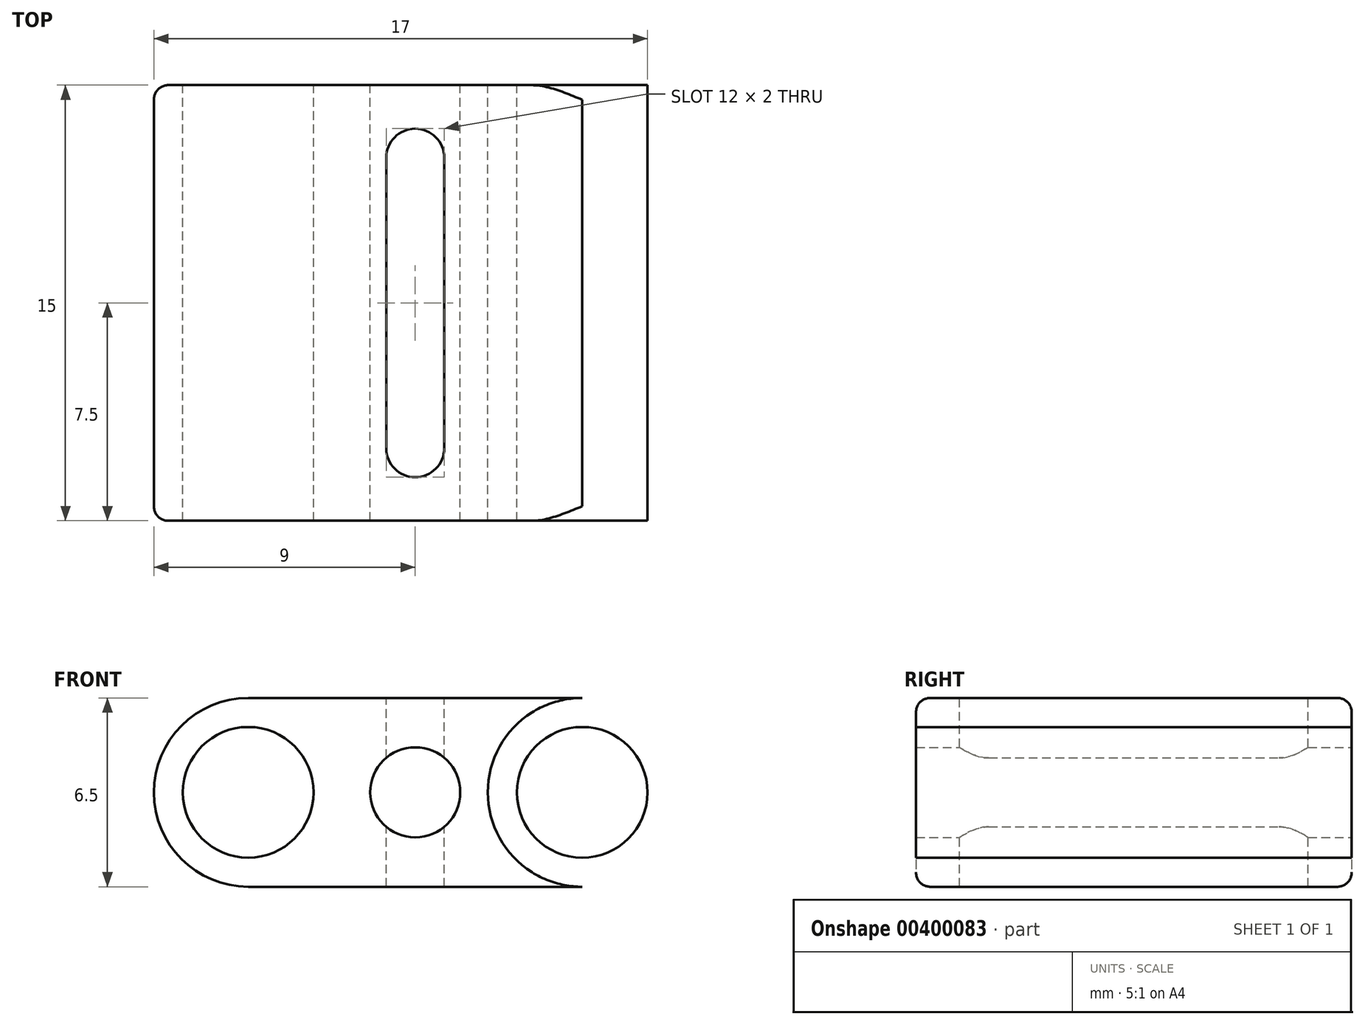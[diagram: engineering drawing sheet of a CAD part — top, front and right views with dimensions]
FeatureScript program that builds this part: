
annotation { "Feature Type Name" : "Feature", "Feature Type Description" : "" }
export const myFeature = defineFeature(function(context is Context, id is Id, definition is map)
    precondition{}
    {
        {
            var Q0;
            Q0=qCreatedBy(makeId("Front.planeOp"),FACE);
            var sketch = newSketch(context, id + "F0", { "sketchPlane" : qUnion([Q0])});
            skLineSegment(sketch, "E0", {"start": v(0, 0) * mm, "end": v(0, 16.22) * mm, "construction": true});
            skCircle(sketch, "E1", {"center": v(-5.75, 0) * mm, "radius": 2.25 * mm});
            skCircle(sketch, "E2.MirrorC", {"center": v(5.75, 0) * mm, "radius": 2.25 * mm});
            skCircle(sketch, "E3", {"center": v(-5.75, 0) * mm, "radius": 3.25 * mm});
            skCircle(sketch, "E4.MirrorC", {"center": v(5.75, 0) * mm, "radius": 3.25 * mm});
            skLineSegment(sketch, "E5", {"start": v(-5.75, 3.25) * mm, "end": v(5.75, 3.25) * mm});
            skLineSegment(sketch, "E6", {"start": v(-5.75, -3.25) * mm, "end": v(5.75, -3.25) * mm});
            skCircle(sketch, "E7", {"center": v(0, 0) * mm, "radius": 1.55 * mm});
            skSolve(sketch);
        }
        {
            var Q0;
            Q0=makeQuery(id+"F0.imprint","IMPRINT",FACE,{"disambiguationData":[TD([[makeQuery(id+"F0.imprint","IMPRINT",EDGE,{"derivedFrom":sQuery(id+"F0.wireOp",EDGE,"E1")}),-1.0]])]});
            var Q1;
            Q1=makeQuery(id+"F0.imprint","IMPRINT",FACE,{"disambiguationData":[TD([[makeQuery(id+"F0.imprint","IMPRINT",EDGE,{"derivedFrom":sQuery(id+"F0.wireOp",EDGE,"E2.MirrorC")}),1.0]])]});
            var Q2;
            {var subQ1=sQuery(id+"F0.wireOp",EDGE,"E5");Q2=makeQuery(id+"F0.imprint","IMPRINT",FACE,{"disambiguationData":[TD([[makeQuery(id+"F0.imprint","IMPRINT",EDGE,{"derivedFrom":subQ1}),-1.0]])]});}
            extrude(context, id + "F1", {"entities" : qUnion([Q0, Q1, Q2]), "depth" : 15 * mm});
        }
        {
            var Q0;
            Q0=makeQuery(id+"F1.opExtrude","SWEPT_FACE",FACE,{"disambiguationData":[OSD([sQuery(id+"F0.wireOp",EDGE,"E5")])]});
            var sketch = newSketch(context, id + "F2", { "sketchPlane" : qUnion([Q0])});
            skLineSegment(sketch, "E8", {"start": v(0, 0) * mm, "end": v(0, -15) * mm, "construction": true});
            skLineSegment(sketch, "E9", {"start": v(0, -7.5) * mm, "end": v(-12.77, -7.5) * mm, "construction": true});
            skCircle(sketch, "E10", {"center": v(0, -12.5) * mm, "radius": 1 * mm});
            skLineSegment(sketch, "E11", {"start": v(-1, -12.5) * mm, "end": v(-1, -7.5) * mm});
            skLineSegment(sketch, "E12", {"start": v(1, -12.5) * mm, "end": v(1, -7.5) * mm});
            skLineSegment(sketch, "E13.MirrorCS", {"start": v(-1, -2.5) * mm, "end": v(-1, -7.5) * mm});
            skCircle(sketch, "E14.MirrorC", {"center": v(0, -2.5) * mm, "radius": 1 * mm});
            skLineSegment(sketch, "E15.MirrorCS", {"start": v(1, -2.5) * mm, "end": v(1, -7.5) * mm});
            skSolve(sketch);
        }
        {
            var Q0;
            Q0 = qSketchRegion(id + "F2", true);
            extrude(context, id + "F3", {"entities" : qUnion([Q0]), "operationType" : NewBodyOperationType.REMOVE, "endBound" : BoundingType.THROUGH_ALL, "oppositeDirection" : true, "depth" : 25 * mm});
        }
        {
            var Q0;
            Q0=makeQuery(id+"F1.opExtrude","CAP_EDGE",EDGE,{"disambiguationData":[OSD([sQuery(id+"F0.wireOp",EDGE,"E5")])],"isStart":true});
            var Q1;
            Q1=makeQuery(id+"F1.opExtrude","CAP_EDGE",EDGE,{"disambiguationData":[OSD([sQuery(id+"F0.wireOp",EDGE,"E5")])],"isStart":false});
            fillet(context, id + "F4", {"entities" : qUnion([Q0, Q1]), "radius" : 0.5 * mm, "tangentPropagation" : true, "allowEdgeOverflow" : false});
        }
    });
